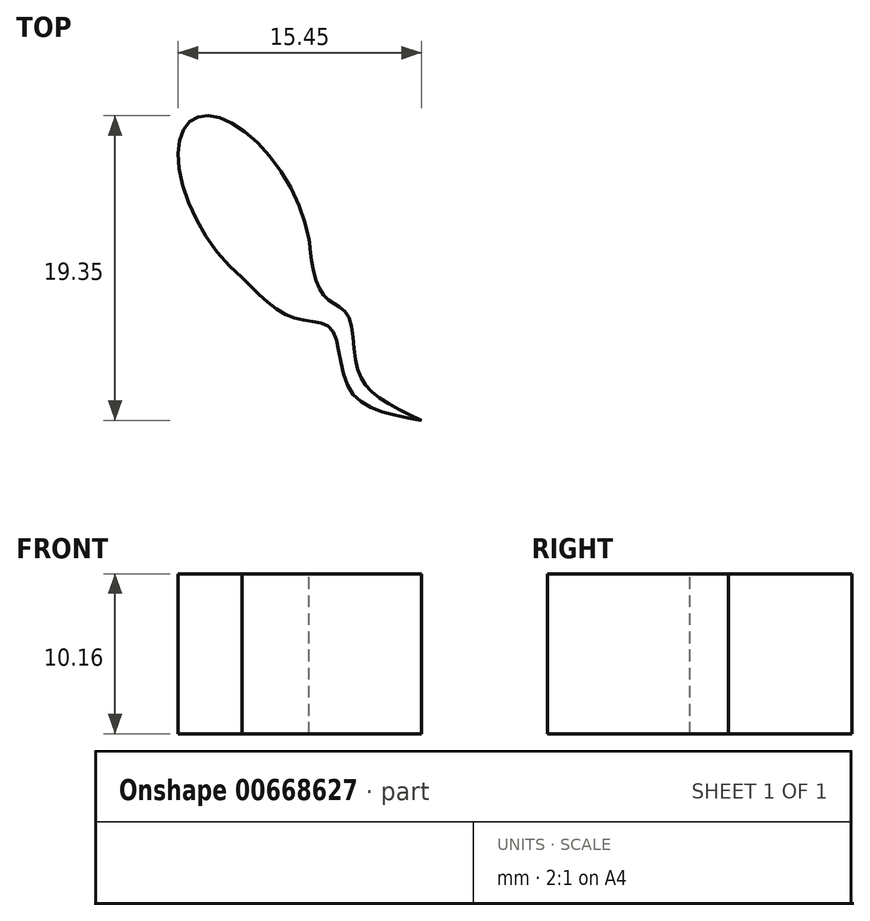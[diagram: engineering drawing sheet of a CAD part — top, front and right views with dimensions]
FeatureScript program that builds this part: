
annotation { "Feature Type Name" : "Feature", "Feature Type Description" : "" }
export const myFeature = defineFeature(function(context is Context, id is Id, definition is map)
    precondition{}
    {
        {
            var Q0;
            Q0=qCreatedBy(makeId("Top.planeOp"),FACE);
            var sketch = newSketch(context, id + "F0", { "sketchPlane" : qUnion([Q0])});
            skEllipticalArc(sketch, "E0", {});
            skPoint(sketch, "E1.1.internal.snap0", {"position": v(-38.81, 19.46) * mm});
            skFitSpline(sketch, "E2", {"points": [v(-42.19, 20.33) * mm, v(-38.86, 17.75) * mm, v(-36.54, 17.08) * mm, v(-35.35, 13.2) * mm, v(-30.8, 11.26) * mm], "startDerivative": vector(12.37, -12.7) * mm, "endDerivative": vector(19.83, -3.41) * mm});
            skFitSpline(sketch, "E3", {"points": [v(-37.94, 22.74) * mm, v(-37.34, 19.77) * mm, v(-36.42, 18.71) * mm, v(-35.47, 17.93) * mm, v(-34.97, 15.02) * mm, v(-33.94, 13.07) * mm, v(-30.8, 11.26) * mm], "startDerivative": vector(2.05, -17.6) * mm, "endDerivative": vector(17.28, -8.19) * mm});
            const initialGuessF0  = {"E0": [-0.04204998537898064, 0.02492324262857437, 0.5102019699118838, -0.8600546202992186, 0.00635, 0.0031117819871955667, 0.7756877069896154, 5.370568062787829]};
            skSetInitialGuess(sketch, initialGuessF0);
            skSolve(sketch);
        }
        {
            var Q0;
            {var subQ0=sQuery(id+"F0.wireOp",EDGE,"E2");Q0=makeQuery(id+"F0.imprint","IMPRINT",FACE,{"disambiguationData":[TD([[makeQuery(id+"F0.imprint","IMPRINT",EDGE,{"derivedFrom":subQ0}),1.0]])]});}
            extrude(context, id + "F1", {"entities" : qUnion([Q0]), "oppositeDirection" : true, "depth" : 10.16 * mm, "offsetDistance" : 25.4 * mm});
        }
    });
